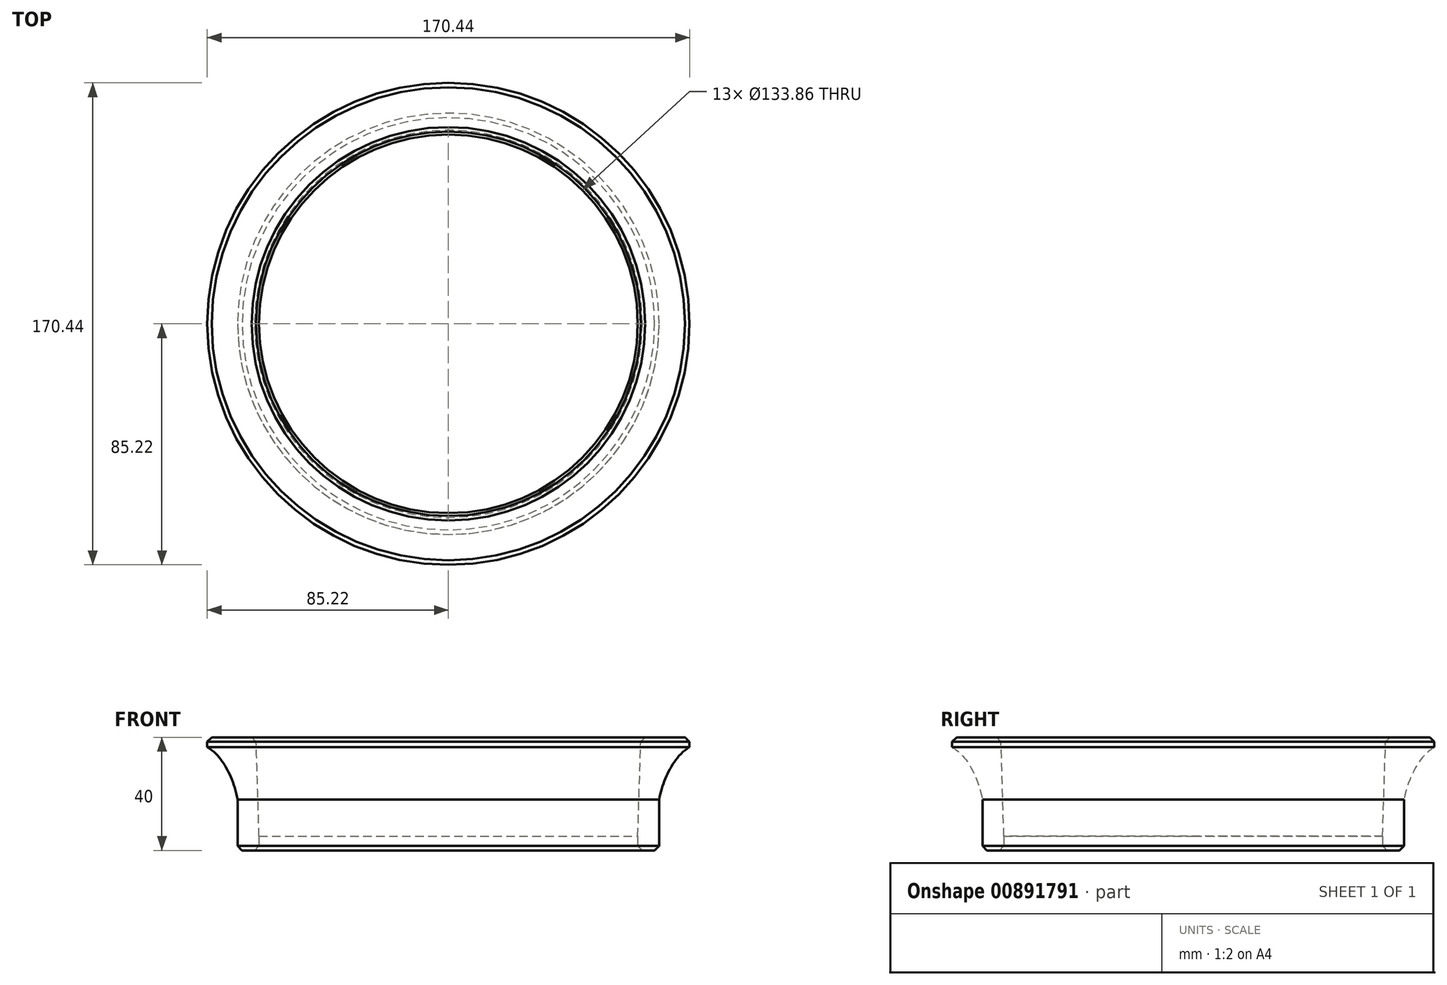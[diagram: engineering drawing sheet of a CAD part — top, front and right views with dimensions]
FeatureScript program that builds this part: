
annotation { "Feature Type Name" : "Feature", "Feature Type Description" : "" }
export const myFeature = defineFeature(function(context is Context, id is Id, definition is map)
    precondition{}
    {
        {
            var Q0;
            Q0=qCreatedBy(makeId("Front.planeOp"),FACE);
            var sketch = newSketch(context, id + "F0", { "sketchPlane" : qUnion([Q0])});
            skLineSegment(sketch, "E0", {"start": v(-74.5, 0) * mm, "end": v(-74.5, 0) * mm});
            skLineSegment(sketch, "E1", {"start": v(-74.5, 0) * mm, "end": v(-74.5, 18) * mm});
            skLineSegment(sketch, "E2", {"start": v(-85.22, 36.5) * mm, "end": v(-85.22, 40) * mm});
            skLineSegment(sketch, "E3", {"start": v(-85.22, 40) * mm, "end": v(-68, 40) * mm});
            skLineSegment(sketch, "E4", {"start": v(0, 0) * mm, "end": v(0, 61.52) * mm, "construction": true});
            skLineSegment(sketch, "E5.top", {"start": v(-67, 0) * mm, "end": v(-66.93, 0) * mm});
            skLineSegment(sketch, "E5.right", {"start": v(-66.93, 5) * mm, "end": v(-66.93, 0) * mm});
            skLineSegment(sketch, "E6.right", {"start": v(-66.93, 5) * mm, "end": v(-66.93, 5) * mm});
            skFitSpline(sketch, "E7", {"points": [v(-74.5, 18) * mm, v(-78.75, 29.58) * mm, v(-85.22, 36.5) * mm], "startDerivative": vector(-4.28, 24.7) * mm, "endDerivative": vector(-19.77, 12.2) * mm});
            skLineSegment(sketch, "E8", {"start": v(-68, 40) * mm, "end": v(-66.93, 5) * mm});
            skPoint(sketch, "E9.end.orphan", {"position": v(-69.93, 0) * mm});
            skLineSegment(sketch, "E10", {"start": v(-74.5, 0) * mm, "end": v(-67, 0) * mm});
            skSolve(sketch);
        }
        {
            var Q0;
            Q0=makeQuery(id+"F0.imprint","IMPRINT",FACE,{"disambiguationData":[TD([[makeQuery(id+"F0.imprint","IMPRINT",EDGE,{"derivedFrom":sQuery(id+"F0.wireOp",EDGE,"E1")}),-1.0]])]});
            var Q1;
            Q1=sQuery(id+"F0.wireOp",EDGE,"E4");
            revolve(context, id + "F1", {"surfaceOperationType" : NewSurfaceOperationType.NEW, "entities" : qUnion([Q0]), "axis" : qUnion([Q1]), "revolveType" : RevolveType.FULL});
        }
        {
            var Q0;
            Q0=makeQuery(id+"F1.opRevolve","SWEPT_FACE",FACE,{"disambiguationData":[OSD([sQuery(id+"F0.wireOp",EDGE,"E5.top"),sQuery(id+"F0.wireOp",EDGE,"E10")])]});
            var Q1;
            Q1=makeQuery(id+"F1.opRevolve","SWEPT_FACE",FACE,{"disambiguationData":[OSD([sQuery(id+"F0.wireOp",EDGE,"E3")])]});
            chamfer(context, id + "F2", {"entities" : qUnion([Q0, Q1]), "width" : 1.6 * mm, "tangentPropagation" : true});
        }
    });
